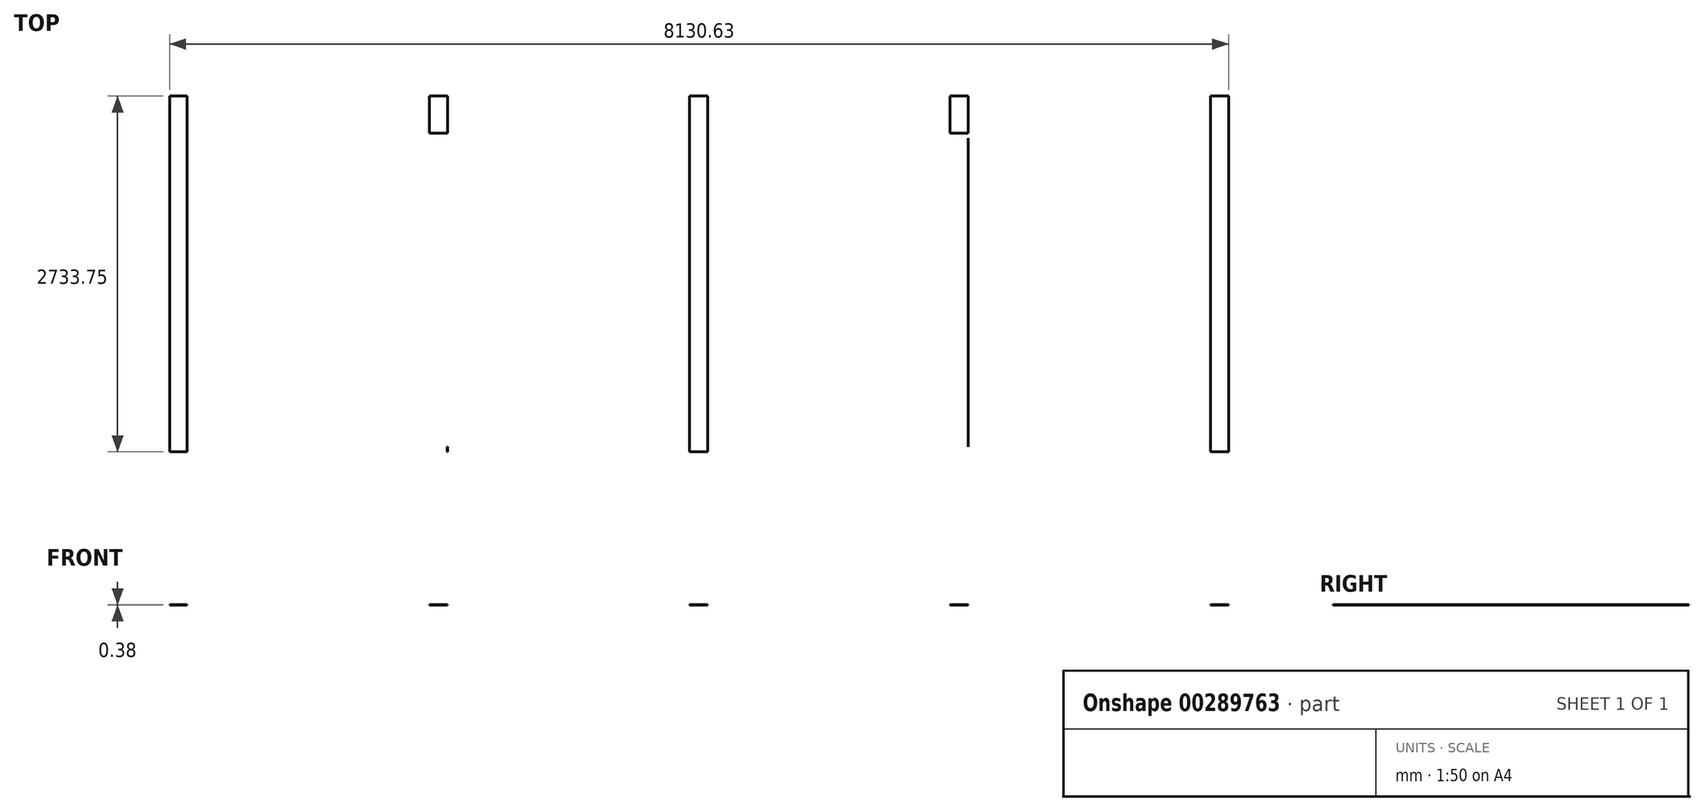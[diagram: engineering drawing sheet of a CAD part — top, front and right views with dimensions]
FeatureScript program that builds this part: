
annotation { "Feature Type Name" : "Feature", "Feature Type Description" : "" }
export const myFeature = defineFeature(function(context is Context, id is Id, definition is map)
    precondition{}
    {
        {
            var Q0;
            Q0=qCreatedBy(makeId("Top.planeOp"),FACE);
            var sketch = newSketch(context, id + "F0", { "sketchPlane" : qUnion([Q0])});
            skLineSegment(sketch, "E0.left", {"start": v(3822.86, -1218.17) * mm, "end": v(3822.86, 1515.58) * mm});
            skLineSegment(sketch, "E1.bottom", {"start": v(-4314.69, -1218.17) * mm, "end": v(3822.86, -1218.17) * mm});
            skLineSegment(sketch, "E2.bottom", {"start": v(3822.86, 1515.58) * mm, "end": v(-245.91, 1515.58) * mm});
            skLineSegment(sketch, "E2.top", {"start": v(3822.86, 1229.83) * mm, "end": v(-245.91, 1229.83) * mm});
            skLineSegment(sketch, "E2.left", {"start": v(3822.86, 1515.58) * mm, "end": v(3822.86, 1229.83) * mm});
            skLineSegment(sketch, "E2.right", {"start": v(-245.91, 1515.58) * mm, "end": v(-245.91, 1229.83) * mm});
            skLineSegment(sketch, "E3", {"start": v(-245.91, 1229.83) * mm, "end": v(-4307.77, 1229.83) * mm});
            skLineSegment(sketch, "E4.bottom", {"start": v(-4307.77, 1229.83) * mm, "end": v(-4168.07, 1229.83) * mm});
            skLineSegment(sketch, "E4.top", {"start": v(-4307.77, -1218.17) * mm, "end": v(-4168.07, -1218.17) * mm});
            skLineSegment(sketch, "E4.left", {"start": v(-4307.77, 1229.83) * mm, "end": v(-4307.77, -1218.17) * mm});
            skLineSegment(sketch, "E4.right", {"start": v(-4168.07, 1229.83) * mm, "end": v(-4168.07, -1218.17) * mm});
            skLineSegment(sketch, "E5.bottom", {"start": v(-315.76, 1229.83) * mm, "end": v(-176.06, 1229.83) * mm});
            skLineSegment(sketch, "E5.top", {"start": v(-315.76, -1218.17) * mm, "end": v(-176.06, -1218.17) * mm});
            skLineSegment(sketch, "E5.left", {"start": v(-315.76, 1229.83) * mm, "end": v(-315.76, -1218.17) * mm});
            skLineSegment(sketch, "E5.right", {"start": v(-176.06, 1229.83) * mm, "end": v(-176.06, -1218.17) * mm});
            skLineSegment(sketch, "E6", {"start": v(-245.91, 1229.83) * mm, "end": v(-245.91, -1218.17) * mm, "construction": true});
            skLineSegment(sketch, "E7.bottom", {"start": v(-2315.25, 1229.83) * mm, "end": v(-2175.55, 1229.83) * mm});
            skLineSegment(sketch, "E7.top", {"start": v(-2315.25, -1218.17) * mm, "end": v(-2175.55, -1218.17) * mm});
            skLineSegment(sketch, "E7.left", {"start": v(-2315.25, 1229.83) * mm, "end": v(-2315.25, -1218.17) * mm});
            skLineSegment(sketch, "E7.right", {"start": v(-2175.55, 1229.83) * mm, "end": v(-2175.55, -1218.17) * mm});
            skLineSegment(sketch, "E8", {"start": v(-4237.92, 1229.83) * mm, "end": v(-4237.92, -1218.17) * mm, "construction": true});
            skLineSegment(sketch, "E9", {"start": v(-2245.4, 1229.83) * mm, "end": v(-2245.4, -1218.17) * mm, "construction": true});
            skLineSegment(sketch, "E10.MirrorCS", {"start": v(3815.94, -1218.17) * mm, "end": v(3676.24, -1218.17) * mm});
            skLineSegment(sketch, "E11.MirrorCS", {"start": v(1823.42, 1229.83) * mm, "end": v(1683.72, 1229.83) * mm});
            skLineSegment(sketch, "E12.MirrorCS", {"start": v(1823.42, -1218.17) * mm, "end": v(1683.72, -1218.17) * mm});
            skLineSegment(sketch, "E13.MirrorCS", {"start": v(3815.94, 1229.83) * mm, "end": v(3676.24, 1229.83) * mm});
            skLineSegment(sketch, "E14.MirrorCS", {"start": v(3815.94, 1229.83) * mm, "end": v(3815.94, -1218.17) * mm});
            skLineSegment(sketch, "E15.MirrorCS", {"start": v(1753.57, 1229.83) * mm, "end": v(1753.57, -1218.17) * mm, "construction": true});
            skLineSegment(sketch, "E16.MirrorCS", {"start": v(1823.42, 1229.83) * mm, "end": v(1823.42, -1218.17) * mm});
            skLineSegment(sketch, "E17.MirrorCS", {"start": v(3746.1, 1229.83) * mm, "end": v(3746.1, -1218.17) * mm, "construction": true});
            skLineSegment(sketch, "E18.MirrorCS", {"start": v(3676.24, 1229.83) * mm, "end": v(3676.24, -1218.17) * mm});
            skLineSegment(sketch, "E19.bottom", {"start": v(-4168.07, -1218.17) * mm, "end": v(-2315.25, -1218.17) * mm});
            skLineSegment(sketch, "E19.top", {"start": v(-4168.07, -1180.07) * mm, "end": v(-2315.25, -1180.07) * mm});
            skLineSegment(sketch, "E19.left", {"start": v(-4168.07, -1218.17) * mm, "end": v(-4168.07, -1180.07) * mm});
            skLineSegment(sketch, "E19.right", {"start": v(-2315.25, -1218.17) * mm, "end": v(-2315.25, -1180.07) * mm});
            skLineSegment(sketch, "E20.bottom", {"start": v(-4168.07, 1229.83) * mm, "end": v(-2315.25, 1229.83) * mm});
            skLineSegment(sketch, "E20.top", {"start": v(-4168.07, 1191.73) * mm, "end": v(-2315.25, 1191.73) * mm});
            skLineSegment(sketch, "E20.left", {"start": v(-4168.07, 1229.83) * mm, "end": v(-4168.07, 1191.73) * mm});
            skLineSegment(sketch, "E20.right", {"start": v(-2315.25, 1229.83) * mm, "end": v(-2315.25, 1191.73) * mm});
            skLineSegment(sketch, "E21.bottom", {"start": v(-4168.07, 1191.73) * mm, "end": v(-4129.97, 1191.73) * mm});
            skLineSegment(sketch, "E21.top", {"start": v(-4168.07, -1180.07) * mm, "end": v(-4129.97, -1180.07) * mm});
            skLineSegment(sketch, "E21.left", {"start": v(-4168.07, 1191.73) * mm, "end": v(-4168.07, -1180.07) * mm});
            skLineSegment(sketch, "E21.right", {"start": v(-4129.97, 1191.73) * mm, "end": v(-4129.97, -1180.07) * mm});
            skLineSegment(sketch, "E22.bottom", {"start": v(-2315.25, 1191.73) * mm, "end": v(-2353.35, 1191.73) * mm});
            skLineSegment(sketch, "E22.top", {"start": v(-2315.25, -1180.07) * mm, "end": v(-2353.35, -1180.07) * mm});
            skLineSegment(sketch, "E22.left", {"start": v(-2315.25, 1191.73) * mm, "end": v(-2315.25, -1180.07) * mm});
            skLineSegment(sketch, "E22.right", {"start": v(-2353.35, 1191.73) * mm, "end": v(-2353.35, -1180.07) * mm});
            skLineSegment(sketch, "E23.bottom", {"start": v(-2759.65, 1191.73) * mm, "end": v(-2721.55, 1191.73) * mm});
            skLineSegment(sketch, "E23.top", {"start": v(-2759.65, -1180.07) * mm, "end": v(-2721.55, -1180.07) * mm});
            skLineSegment(sketch, "E23.left", {"start": v(-2759.65, 1191.73) * mm, "end": v(-2759.65, -1180.07) * mm});
            skLineSegment(sketch, "E23.right", {"start": v(-2721.55, 1191.73) * mm, "end": v(-2721.55, -1180.07) * mm});
            skLineSegment(sketch, "E24.MirrorCS", {"start": v(-2175.55, -1180.07) * mm, "end": v(-2137.45, -1180.07) * mm});
            skLineSegment(sketch, "E25.MirrorCS", {"start": v(-2175.55, -1218.17) * mm, "end": v(-2175.55, -1180.07) * mm});
            skLineSegment(sketch, "E26.MirrorCS", {"start": v(-322.74, -1218.17) * mm, "end": v(-322.74, -1180.07) * mm});
            skLineSegment(sketch, "E27.MirrorCS", {"start": v(-322.74, -1180.07) * mm, "end": v(-360.84, -1180.07) * mm});
            skLineSegment(sketch, "E28.MirrorCS", {"start": v(-322.74, 1191.73) * mm, "end": v(-360.84, 1191.73) * mm});
            skLineSegment(sketch, "E29.MirrorCS", {"start": v(-2175.55, 1229.83) * mm, "end": v(-2175.55, 1191.73) * mm});
            skLineSegment(sketch, "E30.MirrorCS", {"start": v(-2175.55, 1191.73) * mm, "end": v(-2137.45, 1191.73) * mm});
            skLineSegment(sketch, "E31.MirrorCS", {"start": v(-322.74, 1229.83) * mm, "end": v(-322.74, 1191.73) * mm});
            skLineSegment(sketch, "E32.MirrorCS", {"start": v(-512.26, 1191.73) * mm, "end": v(-550.36, 1191.73) * mm});
            skLineSegment(sketch, "E33.MirrorCS", {"start": v(-918.56, -1180.07) * mm, "end": v(-956.66, -1180.07) * mm});
            skLineSegment(sketch, "E34.MirrorCS", {"start": v(-1731.15, 1191.73) * mm, "end": v(-1769.25, 1191.73) * mm});
            skLineSegment(sketch, "E35.MirrorCS", {"start": v(-1324.86, 1191.73) * mm, "end": v(-1362.96, 1191.73) * mm});
            skLineSegment(sketch, "E36.MirrorCS", {"start": v(-918.56, 1191.73) * mm, "end": v(-956.66, 1191.73) * mm});
            skLineSegment(sketch, "E37.MirrorCS", {"start": v(-1731.15, -1180.07) * mm, "end": v(-1769.25, -1180.07) * mm});
            skLineSegment(sketch, "E38.MirrorCS", {"start": v(-512.26, -1180.07) * mm, "end": v(-550.36, -1180.07) * mm});
            skLineSegment(sketch, "E39.MirrorCS", {"start": v(-1324.86, -1180.07) * mm, "end": v(-1362.96, -1180.07) * mm});
            skLineSegment(sketch, "E40.MirrorCS", {"start": v(-322.74, 1191.73) * mm, "end": v(-322.74, -1180.07) * mm});
            skLineSegment(sketch, "E41.MirrorCS", {"start": v(-322.74, -1180.07) * mm, "end": v(-2175.55, -1180.07) * mm});
            skLineSegment(sketch, "E42.MirrorCS", {"start": v(-918.56, 1191.73) * mm, "end": v(-918.56, -1180.07) * mm});
            skLineSegment(sketch, "E43.MirrorCS", {"start": v(-322.74, 1229.83) * mm, "end": v(-2175.55, 1229.83) * mm});
            skLineSegment(sketch, "E44.MirrorCS", {"start": v(-512.26, 1191.73) * mm, "end": v(-512.26, -1180.07) * mm});
            skLineSegment(sketch, "E45.MirrorCS", {"start": v(-360.84, 1191.73) * mm, "end": v(-360.84, -1180.07) * mm});
            skLineSegment(sketch, "E46.MirrorCS", {"start": v(-550.36, 1191.73) * mm, "end": v(-550.36, -1180.07) * mm});
            skLineSegment(sketch, "E47.MirrorCS", {"start": v(-322.74, 1191.73) * mm, "end": v(-2175.55, 1191.73) * mm});
            skLineSegment(sketch, "E48.MirrorCS", {"start": v(-1769.25, 1191.73) * mm, "end": v(-1769.25, -1180.07) * mm});
            skLineSegment(sketch, "E49.MirrorCS", {"start": v(-956.66, 1191.73) * mm, "end": v(-956.66, -1180.07) * mm});
            skLineSegment(sketch, "E50.MirrorCS", {"start": v(-1362.96, 1191.73) * mm, "end": v(-1362.96, -1180.07) * mm});
            skLineSegment(sketch, "E51.MirrorCS", {"start": v(-2175.55, 1191.73) * mm, "end": v(-2175.55, -1180.07) * mm});
            skLineSegment(sketch, "E52.MirrorCS", {"start": v(-322.74, 1229.83) * mm, "end": v(-322.74, -1218.17) * mm});
            skLineSegment(sketch, "E53.MirrorCS", {"start": v(-2137.45, 1191.73) * mm, "end": v(-2137.45, -1180.07) * mm});
            skLineSegment(sketch, "E54.MirrorCS", {"start": v(-1731.15, 1191.73) * mm, "end": v(-1731.15, -1180.07) * mm});
            skLineSegment(sketch, "E55.MirrorCS", {"start": v(-1324.86, 1191.73) * mm, "end": v(-1324.86, -1180.07) * mm});
            skLineSegment(sketch, "E56.MirrorCS", {"start": v(-322.74, -1218.17) * mm, "end": v(-2175.55, -1218.17) * mm});
            skLineSegment(sketch, "E57.MirrorCS", {"start": v(3676.24, -1180.07) * mm, "end": v(3638.14, -1180.07) * mm});
            skLineSegment(sketch, "E58.MirrorCS", {"start": v(3676.24, -1218.17) * mm, "end": v(3676.24, -1180.07) * mm});
            skLineSegment(sketch, "E59.MirrorCS", {"start": v(1823.42, -1218.17) * mm, "end": v(1823.42, -1180.07) * mm});
            skLineSegment(sketch, "E60.MirrorCS", {"start": v(1823.42, 1191.73) * mm, "end": v(1861.52, 1191.73) * mm});
            skLineSegment(sketch, "E61.MirrorCS", {"start": v(3676.24, 1229.83) * mm, "end": v(3676.24, 1191.73) * mm});
            skLineSegment(sketch, "E62.MirrorCS", {"start": v(3676.24, 1191.73) * mm, "end": v(3638.14, 1191.73) * mm});
            skLineSegment(sketch, "E63.MirrorCS", {"start": v(1823.42, -1180.07) * mm, "end": v(1861.52, -1180.07) * mm});
            skLineSegment(sketch, "E64.MirrorCS", {"start": v(1823.42, 1229.83) * mm, "end": v(1823.42, 1191.73) * mm});
            skLineSegment(sketch, "E65.MirrorCS", {"start": v(2267.82, -1180.07) * mm, "end": v(2229.72, -1180.07) * mm});
            skLineSegment(sketch, "E66.MirrorCS", {"start": v(3080.42, 1191.73) * mm, "end": v(3042.32, 1191.73) * mm});
            skLineSegment(sketch, "E67.MirrorCS", {"start": v(3486.72, -1180.07) * mm, "end": v(3448.62, -1180.07) * mm});
            skLineSegment(sketch, "E68.MirrorCS", {"start": v(2674.12, 1191.73) * mm, "end": v(2636.02, 1191.73) * mm});
            skLineSegment(sketch, "E69.MirrorCS", {"start": v(3486.72, 1191.73) * mm, "end": v(3448.62, 1191.73) * mm});
            skLineSegment(sketch, "E70.MirrorCS", {"start": v(2267.82, 1191.73) * mm, "end": v(2229.72, 1191.73) * mm});
            skLineSegment(sketch, "E71.MirrorCS", {"start": v(3080.42, -1180.07) * mm, "end": v(3042.32, -1180.07) * mm});
            skLineSegment(sketch, "E72.MirrorCS", {"start": v(2674.12, -1180.07) * mm, "end": v(2636.02, -1180.07) * mm});
            skLineSegment(sketch, "E73.MirrorCS", {"start": v(3676.24, 1229.83) * mm, "end": v(1823.42, 1229.83) * mm});
            skLineSegment(sketch, "E74.MirrorCS", {"start": v(3676.24, -1218.17) * mm, "end": v(1823.42, -1218.17) * mm});
            skLineSegment(sketch, "E75.MirrorCS", {"start": v(3676.24, 1191.73) * mm, "end": v(3676.24, -1180.07) * mm});
            skLineSegment(sketch, "E76.MirrorCS", {"start": v(1861.52, 1191.73) * mm, "end": v(1861.52, -1180.07) * mm});
            skLineSegment(sketch, "E77.MirrorCS", {"start": v(2229.72, 1191.73) * mm, "end": v(2229.72, -1180.07) * mm});
            skLineSegment(sketch, "E78.MirrorCS", {"start": v(3486.72, 1191.73) * mm, "end": v(3486.72, -1180.07) * mm});
            skLineSegment(sketch, "E79.MirrorCS", {"start": v(3676.24, -1180.07) * mm, "end": v(1823.42, -1180.07) * mm});
            skLineSegment(sketch, "E80.MirrorCS", {"start": v(2674.12, 1191.73) * mm, "end": v(2674.12, -1180.07) * mm});
            skLineSegment(sketch, "E81.MirrorCS", {"start": v(3080.42, 1191.73) * mm, "end": v(3080.42, -1180.07) * mm});
            skLineSegment(sketch, "E82.MirrorCS", {"start": v(3448.62, 1191.73) * mm, "end": v(3448.62, -1180.07) * mm});
            skLineSegment(sketch, "E83.MirrorCS", {"start": v(2267.82, 1191.73) * mm, "end": v(2267.82, -1180.07) * mm});
            skLineSegment(sketch, "E84.MirrorCS", {"start": v(3676.24, 1191.73) * mm, "end": v(1823.42, 1191.73) * mm});
            skLineSegment(sketch, "E85.MirrorCS", {"start": v(1823.42, 1191.73) * mm, "end": v(1823.42, -1180.07) * mm});
            skLineSegment(sketch, "E86.MirrorCS", {"start": v(3638.14, 1191.73) * mm, "end": v(3638.14, -1180.07) * mm});
            skLineSegment(sketch, "E87.MirrorCS", {"start": v(3042.32, 1191.73) * mm, "end": v(3042.32, -1180.07) * mm});
            skLineSegment(sketch, "E88.MirrorCS", {"start": v(-245.91, 1229.83) * mm, "end": v(3815.94, 1229.83) * mm});
            skLineSegment(sketch, "E89.MirrorCS", {"start": v(2636.02, 1191.73) * mm, "end": v(2636.02, -1180.07) * mm});
            skLineSegment(sketch, "E90.left", {"start": v(-176.06, 1191.73) * mm, "end": v(-176.06, 1229.83) * mm});
            skLineSegment(sketch, "E91.top", {"start": v(1645.62, -1180.07) * mm, "end": v(-176.06, -1180.07) * mm});
            skLineSegment(sketch, "E91.right", {"start": v(-176.06, -1218.17) * mm, "end": v(-176.06, -1180.07) * mm});
            skLineSegment(sketch, "E92.bottom", {"start": v(-176.06, 1191.73) * mm, "end": v(-137.96, 1191.73) * mm});
            skLineSegment(sketch, "E92.top", {"start": v(-176.06, -1180.07) * mm, "end": v(-137.96, -1180.07) * mm});
            skLineSegment(sketch, "E92.right", {"start": v(-137.96, 1191.73) * mm, "end": v(-137.96, -1180.07) * mm});
            skLineSegment(sketch, "E93.left", {"start": v(1683.72, 1229.83) * mm, "end": v(1683.72, -1218.17) * mm});
            skLineSegment(sketch, "E94.top", {"start": v(-245.91, 1515.58) * mm, "end": v(-4307.77, 1515.58) * mm});
            skLineSegment(sketch, "E94.left", {"start": v(-245.91, 1229.83) * mm, "end": v(-245.91, 1515.58) * mm});
            skLineSegment(sketch, "E94.right", {"start": v(-4307.77, 1229.83) * mm, "end": v(-4307.77, 1515.58) * mm});
            skLineSegment(sketch, "E95.bottom", {"start": v(-4015.67, -1180.07) * mm, "end": v(-3202.87, -1180.07) * mm});
            skLineSegment(sketch, "E95.top", {"start": v(-4015.67, 591.66) * mm, "end": v(-3202.87, 591.66) * mm});
            skLineSegment(sketch, "E95.left", {"start": v(-4015.67, -1180.07) * mm, "end": v(-4015.67, 591.66) * mm});
            skLineSegment(sketch, "E95.right", {"start": v(-3202.87, -1180.07) * mm, "end": v(-3202.87, 591.66) * mm});
            skLineSegment(sketch, "E96.bottom", {"start": v(-4015.67, 591.66) * mm, "end": v(-4053.77, 591.66) * mm});
            skLineSegment(sketch, "E96.top", {"start": v(-4015.67, -1180.07) * mm, "end": v(-4053.77, -1180.07) * mm});
            skLineSegment(sketch, "E96.left", {"start": v(-4015.67, 591.66) * mm, "end": v(-4015.67, -1180.07) * mm});
            skLineSegment(sketch, "E96.right", {"start": v(-4053.77, 591.66) * mm, "end": v(-4053.77, -1180.07) * mm});
            skLineSegment(sketch, "E97.bottom", {"start": v(-4053.77, -1180.07) * mm, "end": v(-4091.87, -1180.07) * mm});
            skLineSegment(sketch, "E97.top", {"start": v(-4053.77, 1191.73) * mm, "end": v(-4091.87, 1191.73) * mm});
            skLineSegment(sketch, "E97.left", {"start": v(-4053.77, -1180.07) * mm, "end": v(-4053.77, 1191.73) * mm});
            skLineSegment(sketch, "E97.right", {"start": v(-4091.87, -1180.07) * mm, "end": v(-4091.87, 1191.73) * mm});
            skLineSegment(sketch, "E98.bottom", {"start": v(-3202.87, 591.66) * mm, "end": v(-3164.77, 591.66) * mm});
            skLineSegment(sketch, "E98.top", {"start": v(-3202.87, -1180.07) * mm, "end": v(-3164.77, -1180.07) * mm});
            skLineSegment(sketch, "E98.left", {"start": v(-3202.87, 591.66) * mm, "end": v(-3202.87, -1180.07) * mm});
            skLineSegment(sketch, "E98.right", {"start": v(-3164.77, 591.66) * mm, "end": v(-3164.77, -1180.07) * mm});
            skLineSegment(sketch, "E99.bottom", {"start": v(-3164.77, -1180.07) * mm, "end": v(-3126.67, -1180.07) * mm});
            skLineSegment(sketch, "E99.top", {"start": v(-3164.77, 1191.73) * mm, "end": v(-3126.67, 1191.73) * mm});
            skLineSegment(sketch, "E99.left", {"start": v(-3164.77, -1180.07) * mm, "end": v(-3164.77, 1191.73) * mm});
            skLineSegment(sketch, "E99.right", {"start": v(-3126.67, -1180.07) * mm, "end": v(-3126.67, 1191.73) * mm});
            skLineSegment(sketch, "E100.bottom", {"start": v(-3164.77, 591.66) * mm, "end": v(-4053.77, 591.66) * mm});
            skLineSegment(sketch, "E100.top", {"start": v(-3164.77, 629.76) * mm, "end": v(-4053.77, 629.76) * mm});
            skLineSegment(sketch, "E100.left", {"start": v(-3164.77, 591.66) * mm, "end": v(-3164.77, 629.76) * mm});
            skLineSegment(sketch, "E100.right", {"start": v(-4053.77, 591.66) * mm, "end": v(-4053.77, 629.76) * mm});
            skLineSegment(sketch, "E101", {"start": v(-3609.27, 629.76) * mm, "end": v(-3609.27, 1191.73) * mm, "construction": true});
            skLineSegment(sketch, "E102.bottom", {"start": v(-3628.47, 629.76) * mm, "end": v(-3590.07, 629.76) * mm});
            skLineSegment(sketch, "E102.top", {"start": v(-3628.47, 1191.73) * mm, "end": v(-3590.07, 1191.73) * mm});
            skLineSegment(sketch, "E102.left", {"start": v(-3628.47, 629.76) * mm, "end": v(-3628.47, 1191.73) * mm});
            skLineSegment(sketch, "E102.right", {"start": v(-3590.07, 629.76) * mm, "end": v(-3590.07, 1191.73) * mm});
            skLineSegment(sketch, "E103.bottom", {"start": v(-3860.12, 1191.73) * mm, "end": v(-3822.02, 1191.73) * mm});
            skLineSegment(sketch, "E103.top", {"start": v(-3860.12, 629.76) * mm, "end": v(-3822.02, 629.76) * mm});
            skLineSegment(sketch, "E103.left", {"start": v(-3860.12, 1191.73) * mm, "end": v(-3860.12, 629.76) * mm});
            skLineSegment(sketch, "E103.right", {"start": v(-3822.02, 1191.73) * mm, "end": v(-3822.02, 629.76) * mm});
            skLineSegment(sketch, "E104", {"start": v(-3841.07, 1191.73) * mm, "end": v(-3841.07, 629.76) * mm, "construction": true});
            skLineSegment(sketch, "E105.MirrorCS", {"start": v(-3358.42, 1191.73) * mm, "end": v(-3358.42, 629.76) * mm});
            skLineSegment(sketch, "E106.MirrorCS", {"start": v(-3396.52, 1191.73) * mm, "end": v(-3396.52, 629.76) * mm});
            skLineSegment(sketch, "E107", {"start": v(-3202.87, -1180.07) * mm, "end": v(-3202.87, -1218.17) * mm});
            skLineSegment(sketch, "E108", {"start": v(-4015.67, -1180.07) * mm, "end": v(-4015.67, -1218.17) * mm});
            skLineSegment(sketch, "E109.right", {"start": v(1645.62, 1191.73) * mm, "end": v(1645.62, -1218.17) * mm});
            skLineSegment(sketch, "E110", {"start": v(1683.72, 1229.83) * mm, "end": v(1683.72, 1229.83) * mm});
            skLineSegment(sketch, "E111", {"start": v(-137.96, 1191.73) * mm, "end": v(1645.62, 1191.73) * mm});
            skLineSegment(sketch, "E112.bottom", {"start": v(-137.96, 877.33) * mm, "end": v(-99.86, 877.33) * mm});
            skLineSegment(sketch, "E112.top", {"start": v(-137.96, -1180.07) * mm, "end": v(-99.86, -1180.07) * mm});
            skLineSegment(sketch, "E112.left", {"start": v(-137.96, 877.33) * mm, "end": v(-137.96, -1180.07) * mm});
            skLineSegment(sketch, "E112.right", {"start": v(-99.86, 877.33) * mm, "end": v(-99.86, -1180.07) * mm});
            skLineSegment(sketch, "E113.bottom", {"start": v(-137.96, 877.33) * mm, "end": v(916.14, 877.33) * mm});
            skLineSegment(sketch, "E113.top", {"start": v(-137.96, 915.43) * mm, "end": v(916.14, 915.43) * mm});
            skLineSegment(sketch, "E113.left", {"start": v(-137.96, 877.33) * mm, "end": v(-137.96, 915.43) * mm});
            skLineSegment(sketch, "E113.right", {"start": v(916.14, 877.33) * mm, "end": v(916.14, 915.43) * mm});
            skLineSegment(sketch, "E114", {"start": v(878.04, 877.33) * mm, "end": v(878.04, -1218.17) * mm});
            skLineSegment(sketch, "E115.bottom", {"start": v(916.14, 1191.73) * mm, "end": v(954.24, 1191.73) * mm});
            skLineSegment(sketch, "E115.top", {"start": v(916.14, -1180.07) * mm, "end": v(954.24, -1180.07) * mm});
            skLineSegment(sketch, "E115.left", {"start": v(916.14, 1191.73) * mm, "end": v(916.14, -1180.07) * mm});
            skLineSegment(sketch, "E115.right", {"start": v(954.24, 1191.73) * mm, "end": v(954.24, -1180.07) * mm});
            skLineSegment(sketch, "E116", {"start": v(389.09, 915.43) * mm, "end": v(389.09, 1191.73) * mm, "construction": true});
            skLineSegment(sketch, "E117.bottom", {"start": v(369.88, 1191.73) * mm, "end": v(408.29, 1191.73) * mm});
            skLineSegment(sketch, "E117.top", {"start": v(369.88, 915.43) * mm, "end": v(408.29, 915.43) * mm});
            skLineSegment(sketch, "E117.left", {"start": v(369.88, 1191.73) * mm, "end": v(369.88, 915.43) * mm});
            skLineSegment(sketch, "E117.right", {"start": v(408.29, 1191.73) * mm, "end": v(408.29, 915.43) * mm});
            skLineSegment(sketch, "E118.bottom", {"start": v(96.94, 915.43) * mm, "end": v(135.04, 915.43) * mm});
            skLineSegment(sketch, "E118.top", {"start": v(96.94, 1191.73) * mm, "end": v(135.04, 1191.73) * mm});
            skLineSegment(sketch, "E118.left", {"start": v(96.94, 915.43) * mm, "end": v(96.94, 1191.73) * mm});
            skLineSegment(sketch, "E118.right", {"start": v(135.04, 915.43) * mm, "end": v(135.04, 1191.73) * mm});
            skLineSegment(sketch, "E119", {"start": v(115.99, 1191.73) * mm, "end": v(115.99, 915.43) * mm, "construction": true});
            skLineSegment(sketch, "E120.MirrorCS", {"start": v(681.24, 1191.73) * mm, "end": v(643.14, 1191.73) * mm});
            skLineSegment(sketch, "E121.MirrorCS", {"start": v(681.24, 915.43) * mm, "end": v(643.14, 915.43) * mm});
            skLineSegment(sketch, "E122.MirrorCS", {"start": v(643.14, 915.43) * mm, "end": v(643.14, 1191.73) * mm});
            skLineSegment(sketch, "E123.MirrorCS", {"start": v(662.19, 1191.73) * mm, "end": v(662.19, 915.43) * mm, "construction": true});
            skLineSegment(sketch, "E124.MirrorCS", {"start": v(681.24, 915.43) * mm, "end": v(681.24, 1191.73) * mm});
            skLineSegment(sketch, "E125.bottom", {"start": v(1322.43, 1191.73) * mm, "end": v(1360.53, 1191.73) * mm});
            skLineSegment(sketch, "E125.top", {"start": v(1322.43, -1180.07) * mm, "end": v(1360.53, -1180.07) * mm});
            skLineSegment(sketch, "E125.left", {"start": v(1322.43, 1191.73) * mm, "end": v(1322.43, -1180.07) * mm});
            skLineSegment(sketch, "E125.right", {"start": v(1360.53, 1191.73) * mm, "end": v(1360.53, -1180.07) * mm});
            skLineSegment(sketch, "E126", {"start": v(-99.86, -1180.07) * mm, "end": v(-99.86, -1218.17) * mm});
            skSolve(sketch);
        }
        {
            var Q0;
            {var subQ3=sQuery(id+"F0.wireOp",EDGE,"jjNAWN9L-icPI-AxbA-Y6Pq-o1EGEALKaFy1");var subQ5=sQuery(id+"F0.wireOp",EDGE,"5f963c61-5f66-4834-8852-3989dfd0aaaa0.MirrorCS");var subQ6=makeQuery(id+"F0.imprint","INTERSECT",VERTEX,{"derivedFrom":[subQ5,subQ3]});Q0=makeQuery(id+"F0.imprint","IMPRINT",FACE,{"disambiguationData":[TD([[makeQuery(id+"F0.imprint","IMPRINT",EDGE,{"disambiguationData":[TD([[subQ6,-1.0]])],"derivedFrom":subQ5}),-1.0]])]});}
            var Q1;
            {var subQ1=sQuery(id+"F0.wireOp",EDGE,"c3f41723-229c-4d74-ac07-4786d7f9cf2e0.MirrorCS");var subQ5=sQuery(id+"F0.wireOp",EDGE,"jjNAWN9L-icPI-AxbA-Y6Pq-o1EGEALKaFy1");var subQ7=makeQuery(id+"F0.imprint","INTERSECT",VERTEX,{"derivedFrom":[subQ1,subQ5]});Q1=makeQuery(id+"F0.imprint","IMPRINT",FACE,{"disambiguationData":[TD([[makeQuery(id+"F0.imprint","IMPRINT",EDGE,{"disambiguationData":[TD([[subQ7,-1.0]])],"derivedFrom":subQ1}),1.0]])]});}
            var Q2;
            {var subQ5=sQuery(id+"F0.wireOp",EDGE,"lJZTp2Bh-KL5G-mgcu-Pd3p-ZrVlOJJElSC5");Q2=makeQuery(id+"F0.imprint","IMPRINT",FACE,{"disambiguationData":[TD([[makeQuery(id+"F0.imprint","IMPRINT",EDGE,{"derivedFrom":subQ5}),1.0]])]});}
            var Q3;
            {var subQ0=sQuery(id+"F0.wireOp",EDGE,"1XwIb5Eg-bF9u-TIWm-DKcX-weKEORKnCqGm.right");Q3=makeQuery(id+"F0.imprint","IMPRINT",FACE,{"disambiguationData":[TD([[makeQuery(id+"F0.imprint","IMPRINT",EDGE,{"derivedFrom":subQ0}),-1.0]])]});}
            var Q4;
            {var subQ0=sQuery(id+"F0.wireOp",EDGE,"edbdd21b-7951-4497-ac7e-6e46abb4ccd70.MirrorCS");Q4=makeQuery(id+"F0.imprint","IMPRINT",FACE,{"disambiguationData":[TD([[makeQuery(id+"F0.imprint","IMPRINT",EDGE,{"derivedFrom":subQ0}),-1.0]])]});}
            var Q5;
            {var subQ0=sQuery(id+"F0.wireOp",EDGE,"573c87d8-b675-496e-a079-9395e3357b8d0.MirrorCS");Q5=makeQuery(id+"F0.imprint","IMPRINT",FACE,{"disambiguationData":[TD([[makeQuery(id+"F0.imprint","IMPRINT",EDGE,{"derivedFrom":subQ0}),1.0]])]});}
            var Q6;
            {var subQ0=sQuery(id+"F0.wireOp",EDGE,"7de17b8e-8469-475a-b975-fd82b060c23f0.MirrorCS");Q6=makeQuery(id+"F0.imprint","IMPRINT",FACE,{"disambiguationData":[TD([[makeQuery(id+"F0.imprint","IMPRINT",EDGE,{"derivedFrom":subQ0}),1.0]])]});}
            var Q7;
            {var subQ0=sQuery(id+"F0.wireOp",EDGE,"9fe0fe99-07bc-4679-9664-f55d6f2dc43d0.MirrorCS");Q7=makeQuery(id+"F0.imprint","IMPRINT",FACE,{"disambiguationData":[TD([[makeQuery(id+"F0.imprint","IMPRINT",EDGE,{"derivedFrom":subQ0}),1.0]])]});}
            var Q8;
            {var subQ0=sQuery(id+"F0.wireOp",EDGE,"b7a96eb8-1ea0-4e2f-8a00-b5aa0dec934b0.MirrorCS");Q8=makeQuery(id+"F0.imprint","IMPRINT",FACE,{"disambiguationData":[TD([[makeQuery(id+"F0.imprint","IMPRINT",EDGE,{"derivedFrom":subQ0}),-1.0]])]});}
            var Q9;
            {var subQ0=sQuery(id+"F0.wireOp",EDGE,"e03bbd14-4e46-43d8-a5f9-80b2dea7db7f0.MirrorCS");Q9=makeQuery(id+"F0.imprint","IMPRINT",FACE,{"disambiguationData":[TD([[makeQuery(id+"F0.imprint","IMPRINT",EDGE,{"derivedFrom":subQ0}),1.0]])]});}
            var Q10;
            {var subQ5=sQuery(id+"F0.wireOp",EDGE,"0632b321-56e7-4b31-9cd1-585e07a893ff0.MirrorCS");var subQ6=sQuery(id+"F0.wireOp",EDGE,"1XwIb5Eg-bF9u-TIWm-DKcX-weKEORKnCqGm.bottom");var subQ7=makeQuery(id+"F0.imprint","INTERSECT",VERTEX,{"derivedFrom":[subQ6,subQ5]});Q10=makeQuery(id+"F0.imprint","IMPRINT",FACE,{"disambiguationData":[TD([[makeQuery(id+"F0.imprint","IMPRINT",EDGE,{"disambiguationData":[TD([[subQ7,-1.0]])],"derivedFrom":subQ6}),-1.0]])]});}
            var Q11;
            Q11=makeQuery(id+"F0.imprint","IMPRINT",FACE,{"disambiguationData":[TD([[makeQuery(id+"F0.imprint","IMPRINT",EDGE,{"derivedFrom":sQuery(id+"F0.wireOp",EDGE,"w7in2STq-dmfq-Ztst-uc13-PS53EKAe34f7.bottom")}),-1.0]])]});
            var Q12;
            {var subQ4=sQuery(id+"F0.wireOp",EDGE,"019fe33c-2ba7-4981-a1aa-b8912489248e0.MirrorCS");var subQ6=sQuery(id+"F0.wireOp",EDGE,"1XwIb5Eg-bF9u-TIWm-DKcX-weKEORKnCqGm.bottom");var subQ7=makeQuery(id+"F0.imprint","INTERSECT",VERTEX,{"derivedFrom":[subQ6,subQ4]});Q12=makeQuery(id+"F0.imprint","IMPRINT",FACE,{"disambiguationData":[TD([[makeQuery(id+"F0.imprint","IMPRINT",EDGE,{"disambiguationData":[TD([[subQ7,-1.0]])],"derivedFrom":subQ6}),-1.0]])]});}
            var Q13;
            {var subQ5=sQuery(id+"F0.wireOp",EDGE,"E1.right");Q13=makeQuery(id+"F0.imprint","IMPRINT",FACE,{"disambiguationData":[TD([[makeQuery(id+"F0.imprint","IMPRINT",EDGE,{"derivedFrom":subQ5}),1.0]])]});}
            var Q14;
            {var subQ4=sQuery(id+"F0.wireOp",EDGE,"8a681850-bd4a-4ca6-8d45-30870cc5114b0.MirrorCS");var subQ6=sQuery(id+"F0.wireOp",EDGE,"1XwIb5Eg-bF9u-TIWm-DKcX-weKEORKnCqGm.bottom");var subQ7=makeQuery(id+"F0.imprint","INTERSECT",VERTEX,{"derivedFrom":[subQ6,subQ4]});Q14=makeQuery(id+"F0.imprint","IMPRINT",FACE,{"disambiguationData":[TD([[makeQuery(id+"F0.imprint","IMPRINT",EDGE,{"disambiguationData":[TD([[subQ7,-1.0]])],"derivedFrom":subQ6}),-1.0]])]});}
            var Q15;
            {var subQ4=sQuery(id+"F0.wireOp",EDGE,"1XwIb5Eg-bF9u-TIWm-DKcX-weKEORKnCqGm.left");Q15=makeQuery(id+"F0.imprint","IMPRINT",FACE,{"disambiguationData":[TD([[makeQuery(id+"F0.imprint","IMPRINT",EDGE,{"derivedFrom":subQ4}),1.0]])]});}
            var Q16;
            {var subQ5=sQuery(id+"F0.wireOp",EDGE,"1XwIb5Eg-bF9u-TIWm-DKcX-weKEORKnCqGm.bottom");var subQ11=sQuery(id+"F0.wireOp",EDGE,"f7381abf-e9df-4e1a-a30e-4fe6b1d368c50.MirrorCS");var subQ12=makeQuery(id+"F0.imprint","INTERSECT",VERTEX,{"derivedFrom":[subQ5,subQ11]});Q16=makeQuery(id+"F0.imprint","IMPRINT",FACE,{"disambiguationData":[TD([[makeQuery(id+"F0.imprint","IMPRINT",EDGE,{"disambiguationData":[TD([[subQ12,-1.0]])],"derivedFrom":subQ5}),-1.0]])]});}
            var Q17;
            {var subQ6=sQuery(id+"F0.wireOp",EDGE,"E1.left");Q17=makeQuery(id+"F0.imprint","IMPRINT",FACE,{"disambiguationData":[TD([[makeQuery(id+"F0.imprint","IMPRINT",EDGE,{"derivedFrom":subQ6}),-1.0]])]});}
            var Q18;
            {var subQ6=sQuery(id+"F0.wireOp",EDGE,"5OPExjK1-Sqdo-9fgj-zmjT-l9LixJuiSe1q");Q18=makeQuery(id+"F0.imprint","IMPRINT",FACE,{"disambiguationData":[TD([[makeQuery(id+"F0.imprint","IMPRINT",EDGE,{"derivedFrom":subQ6}),-1.0]])]});}
            var Q19;
            {var subQ0=sQuery(id+"F0.wireOp",EDGE,"95ca570f-170f-43a6-b84c-d3a65055c82b0.MirrorCS");Q19=makeQuery(id+"F0.imprint","IMPRINT",FACE,{"disambiguationData":[TD([[makeQuery(id+"F0.imprint","IMPRINT",EDGE,{"derivedFrom":subQ0}),1.0]])]});}
            var Q20;
            {var subQ3=sQuery(id+"F0.wireOp",EDGE,"eca8af08-4f88-4f9e-b7fb-055b73c8b4f30.MirrorCS");var subQ4=sQuery(id+"F0.wireOp",EDGE,"1XwIb5Eg-bF9u-TIWm-DKcX-weKEORKnCqGm.bottom");var subQ5=makeQuery(id+"F0.imprint","INTERSECT",VERTEX,{"derivedFrom":[subQ4,subQ3]});Q20=makeQuery(id+"F0.imprint","IMPRINT",FACE,{"disambiguationData":[TD([[makeQuery(id+"F0.imprint","IMPRINT",EDGE,{"disambiguationData":[TD([[subQ5,-1.0]])],"derivedFrom":subQ4}),-1.0]])]});}
            var Q21;
            {var subQ0=sQuery(id+"F0.wireOp",EDGE,"1XwIb5Eg-bF9u-TIWm-DKcX-weKEORKnCqGm.right");Q21=makeQuery(id+"F0.imprint","IMPRINT",FACE,{"disambiguationData":[TD([[makeQuery(id+"F0.imprint","IMPRINT",EDGE,{"derivedFrom":subQ0}),-1.0]])]});}
            var Q22;
            {var subQ7=sQuery(id+"F0.wireOp",EDGE,"7E0FlCXR-JigA-jfUJ-zGrG-kKcglUNU7Liy");Q22=makeQuery(id+"F0.imprint","IMPRINT",FACE,{"disambiguationData":[TD([[makeQuery(id+"F0.imprint","IMPRINT",EDGE,{"derivedFrom":subQ7}),-1.0]])]});}
            var Q23;
            {var subQ4=sQuery(id+"F0.wireOp",EDGE,"1bcce820-757c-45ce-a4fe-54bff22ba8310.MirrorCS");var subQ5=sQuery(id+"F0.wireOp",EDGE,"1XwIb5Eg-bF9u-TIWm-DKcX-weKEORKnCqGm.bottom");var subQ6=makeQuery(id+"F0.imprint","INTERSECT",VERTEX,{"derivedFrom":[subQ5,subQ4]});Q23=makeQuery(id+"F0.imprint","IMPRINT",FACE,{"disambiguationData":[TD([[makeQuery(id+"F0.imprint","IMPRINT",EDGE,{"disambiguationData":[TD([[subQ6,-1.0]])],"derivedFrom":subQ5}),-1.0]])]});}
            var Q24;
            Q24=makeQuery(id+"F0.imprint","IMPRINT",FACE,{"disambiguationData":[TD([[makeQuery(id+"F0.imprint","IMPRINT",EDGE,{"derivedFrom":sQuery(id+"F0.wireOp",EDGE,"xTM1oSQN-q9p7-LrQJ-wgkP-syFjsQtJfwuK.bottom")}),-1.0]])]});
            var Q25;
            {var subQ0=sQuery(id+"F0.wireOp",EDGE,"1b0e9755-274d-47f2-9ad2-c5868fe4f0aa0.MirrorCS");Q25=makeQuery(id+"F0.imprint","IMPRINT",FACE,{"disambiguationData":[TD([[makeQuery(id+"F0.imprint","IMPRINT",EDGE,{"derivedFrom":subQ0}),1.0]])]});}
            var Q26;
            {var subQ0=sQuery(id+"F0.wireOp",EDGE,"2c59450c-3f31-460a-8c07-403c14a947670.MirrorCS");Q26=makeQuery(id+"F0.imprint","IMPRINT",FACE,{"disambiguationData":[TD([[makeQuery(id+"F0.imprint","IMPRINT",EDGE,{"derivedFrom":subQ0}),1.0]])]});}
            var Q27;
            {var subQ0=sQuery(id+"F0.wireOp",EDGE,"1b9fc814-7275-47f6-8dd0-aeae657b9ac90.MirrorCS");Q27=makeQuery(id+"F0.imprint","IMPRINT",FACE,{"disambiguationData":[TD([[makeQuery(id+"F0.imprint","IMPRINT",EDGE,{"derivedFrom":subQ0}),1.0]])]});}
            var Q28;
            {var subQ0=sQuery(id+"F0.wireOp",EDGE,"0493b29f-ec4a-4c4c-ac9e-8fdb3be76d310.MirrorCS");Q28=makeQuery(id+"F0.imprint","IMPRINT",FACE,{"disambiguationData":[TD([[makeQuery(id+"F0.imprint","IMPRINT",EDGE,{"derivedFrom":subQ0}),1.0]])]});}
            var Q29;
            {var subQ0=sQuery(id+"F0.wireOp",EDGE,"63c733ed-a5aa-43e7-ab23-9ab8c604324c0.MirrorCS");Q29=makeQuery(id+"F0.imprint","IMPRINT",FACE,{"disambiguationData":[TD([[makeQuery(id+"F0.imprint","IMPRINT",EDGE,{"derivedFrom":subQ0}),1.0]])]});}
            var Q30;
            Q30=makeQuery(id+"F0.imprint","IMPRINT",FACE,{"disambiguationData":[TD([[makeQuery(id+"F0.imprint","IMPRINT",EDGE,{"derivedFrom":sQuery(id+"F0.wireOp",EDGE,"3EoNbSYs-SzWb-u8DF-ybgV-jMauNVkNRy9z.bottom")}),1.0]])]});
            var Q31;
            {var subQ0=sQuery(id+"F0.wireOp",EDGE,"T9lHoMTv-QEzR-Dyhh-EcdA-VJLsKytDJrYi");Q31=makeQuery(id+"F0.imprint","IMPRINT",FACE,{"disambiguationData":[TD([[makeQuery(id+"F0.imprint","IMPRINT",EDGE,{"derivedFrom":subQ0}),1.0]])]});}
            var Q32;
            {var subQ0=sQuery(id+"F0.wireOp",EDGE,"e8148a9c-46db-40cc-98a3-4964df314f830.MirrorCS");Q32=makeQuery(id+"F0.imprint","IMPRINT",FACE,{"disambiguationData":[TD([[makeQuery(id+"F0.imprint","IMPRINT",EDGE,{"derivedFrom":subQ0}),-1.0]])]});}
            var Q33;
            {var subQ6=sQuery(id+"F0.wireOp",EDGE,"sNmUnq7e-THn6-FXXE-0TdV-tI3yUDcPX31l");Q33=makeQuery(id+"F0.imprint","IMPRINT",FACE,{"disambiguationData":[TD([[makeQuery(id+"F0.imprint","IMPRINT",EDGE,{"derivedFrom":subQ6}),1.0]])]});}
            var Q34;
            {var subQ0=sQuery(id+"F0.wireOp",EDGE,"TX6lwSvD-SgXL-Km0w-BdGv-l82Iv6GDQNNj");Q34=makeQuery(id+"F0.imprint","IMPRINT",FACE,{"disambiguationData":[TD([[makeQuery(id+"F0.imprint","IMPRINT",EDGE,{"derivedFrom":subQ0}),1.0]])]});}
            var Q35;
            {var subQ5=sQuery(id+"F0.wireOp",EDGE,"lJZTp2Bh-KL5G-mgcu-Pd3p-ZrVlOJJElSC5");Q35=makeQuery(id+"F0.imprint","IMPRINT",FACE,{"disambiguationData":[TD([[makeQuery(id+"F0.imprint","IMPRINT",EDGE,{"derivedFrom":subQ5}),1.0]])]});}
            var Q36;
            {var subQ3=sQuery(id+"F0.wireOp",EDGE,"7Q4NYOsG-TNh0-UE7v-idsB-Km2WiAvK161E");Q36=makeQuery(id+"F0.imprint","IMPRINT",FACE,{"disambiguationData":[TD([[makeQuery(id+"F0.imprint","IMPRINT",EDGE,{"derivedFrom":subQ3}),1.0]])]});}
            var Q37;
            {var subQ5=sQuery(id+"F0.wireOp",EDGE,"lJZTp2Bh-KL5G-mgcu-Pd3p-ZrVlOJJElSC5");Q37=makeQuery(id+"F0.imprint","IMPRINT",FACE,{"disambiguationData":[TD([[makeQuery(id+"F0.imprint","IMPRINT",EDGE,{"derivedFrom":subQ5}),1.0]])]});}
            var Q38;
            {var subQ6=sQuery(id+"F0.wireOp",EDGE,"5OPExjK1-Sqdo-9fgj-zmjT-l9LixJuiSe1q");Q38=makeQuery(id+"F0.imprint","IMPRINT",FACE,{"disambiguationData":[TD([[makeQuery(id+"F0.imprint","IMPRINT",EDGE,{"derivedFrom":subQ6}),-1.0]])]});}
            var Q39;
            {var subQ3=sQuery(id+"F0.wireOp",EDGE,"kb0NHO8k-GRdv-KMOx-osSm-lJc2wDgV5qJY");Q39=makeQuery(id+"F0.imprint","IMPRINT",FACE,{"disambiguationData":[TD([[makeQuery(id+"F0.imprint","IMPRINT",EDGE,{"derivedFrom":subQ3}),1.0]])]});}
            var Q40;
            {var subQ0=sQuery(id+"F0.wireOp",EDGE,"n8L3RjNa-mBsY-hc5F-DRgW-xquJLlsyQC8t");var subQ1=sQuery(id+"F0.wireOp",EDGE,"019fe33c-2ba7-4981-a1aa-b8912489248e0.MirrorCS");var subQ2=makeQuery(id+"F0.imprint","INTERSECT",VERTEX,{"derivedFrom":[subQ1,subQ0]});Q40=makeQuery(id+"F0.imprint","IMPRINT",FACE,{"disambiguationData":[TD([[makeQuery(id+"F0.imprint","IMPRINT",EDGE,{"disambiguationData":[TD([[subQ2,-1.0]])],"derivedFrom":subQ1}),-1.0]])]});}
            var Q41;
            {var subQ6=sQuery(id+"F0.wireOp",EDGE,"5OPExjK1-Sqdo-9fgj-zmjT-l9LixJuiSe1q");Q41=makeQuery(id+"F0.imprint","IMPRINT",FACE,{"disambiguationData":[TD([[makeQuery(id+"F0.imprint","IMPRINT",EDGE,{"derivedFrom":subQ6}),-1.0]])]});}
            var Q42;
            {var subQ0=sQuery(id+"F0.wireOp",EDGE,"0e344b7f-dcc7-4a3f-8939-196222c3ee7a0.MirrorCS");Q42=makeQuery(id+"F0.imprint","IMPRINT",FACE,{"disambiguationData":[TD([[makeQuery(id+"F0.imprint","IMPRINT",EDGE,{"derivedFrom":subQ0}),-1.0]])]});}
            var Q43;
            {var subQ0=sQuery(id+"F0.wireOp",EDGE,"Bkj7O7oP-ktTF-DsHg-vzrG-3IRV2kZJSDV0");var subQ5=sQuery(id+"F0.wireOp",EDGE,"E1.top");var subQ8=makeQuery(id+"F0.imprint","INTERSECT",VERTEX,{"derivedFrom":[subQ5,subQ0]});Q43=makeQuery(id+"F0.imprint","IMPRINT",FACE,{"disambiguationData":[TD([[makeQuery(id+"F0.imprint","IMPRINT",EDGE,{"disambiguationData":[TD([[subQ8,-1.0]])],"derivedFrom":subQ5}),1.0]])]});}
            var Q44;
            {var subQ0=sQuery(id+"F0.wireOp",EDGE,"jjNAWN9L-icPI-AxbA-Y6Pq-o1EGEALKaFy1");var subQ1=sQuery(id+"F0.wireOp",EDGE,"eaf639a9-24cc-49c5-a44c-8973cc1609e50.MirrorCS");var subQ2=makeQuery(id+"F0.imprint","INTERSECT",VERTEX,{"derivedFrom":[subQ1,subQ0]});Q44=makeQuery(id+"F0.imprint","IMPRINT",FACE,{"disambiguationData":[TD([[makeQuery(id+"F0.imprint","IMPRINT",EDGE,{"disambiguationData":[TD([[subQ2,-1.0]])],"derivedFrom":subQ1}),1.0]])]});}
            var Q45;
            Q45=makeQuery(id+"F0.imprint","IMPRINT",FACE,{"disambiguationData":[TD([[makeQuery(id+"F0.imprint","IMPRINT",EDGE,{"derivedFrom":sQuery(id+"F0.wireOp",EDGE,"E4.bottom")}),-1.0]])]});
            var Q46;
            Q46=makeQuery(id+"F0.imprint","IMPRINT",FACE,{"disambiguationData":[TD([[makeQuery(id+"F0.imprint","IMPRINT",EDGE,{"derivedFrom":sQuery(id+"F0.wireOp",EDGE,"E21.bottom")}),-1.0]])]});
            var Q47;
            Q47=makeQuery(id+"F0.imprint","IMPRINT",FACE,{"disambiguationData":[TD([[makeQuery(id+"F0.imprint","IMPRINT",EDGE,{"derivedFrom":sQuery(id+"F0.wireOp",EDGE,"E20.bottom")}),-1.0]])]});
            var Q48;
            Q48=makeQuery(id+"F0.imprint","IMPRINT",FACE,{"disambiguationData":[TD([[makeQuery(id+"F0.imprint","IMPRINT",EDGE,{"derivedFrom":sQuery(id+"F0.wireOp",EDGE,"V0uafj4D-blUL-0R42-RDYG-w4zu7gxU5Okz.bottom")}),-1.0]])]});
            var Q49;
            Q49=makeQuery(id+"F0.imprint","IMPRINT",FACE,{"disambiguationData":[TD([[makeQuery(id+"F0.imprint","IMPRINT",EDGE,{"derivedFrom":sQuery(id+"F0.wireOp",EDGE,"tgIF31wR-Pcny-3N63-f3Ax-q6FNio27vSr7.bottom")}),-1.0]])]});
            var Q50;
            Q50=makeQuery(id+"F0.imprint","IMPRINT",FACE,{"disambiguationData":[TD([[makeQuery(id+"F0.imprint","IMPRINT",EDGE,{"derivedFrom":sQuery(id+"F0.wireOp",EDGE,"tej6zg4S-c0JJ-q25J-w4bm-2LaaiJUFbgIA.bottom")}),-1.0]])]});
            var Q51;
            Q51=makeQuery(id+"F0.imprint","IMPRINT",FACE,{"disambiguationData":[TD([[makeQuery(id+"F0.imprint","IMPRINT",EDGE,{"derivedFrom":sQuery(id+"F0.wireOp",EDGE,"E23.bottom")}),-1.0]])]});
            var Q52;
            Q52=makeQuery(id+"F0.imprint","IMPRINT",FACE,{"disambiguationData":[TD([[makeQuery(id+"F0.imprint","IMPRINT",EDGE,{"derivedFrom":sQuery(id+"F0.wireOp",EDGE,"E22.bottom")}),1.0]])]});
            var Q53;
            {var subQ2=sQuery(id+"F0.wireOp",EDGE,"E7.bottom");Q53=makeQuery(id+"F0.imprint","IMPRINT",FACE,{"disambiguationData":[TD([[makeQuery(id+"F0.imprint","IMPRINT",EDGE,{"derivedFrom":subQ2}),-1.0]])]});}
            var Q54;
            {var subQ3=sQuery(id+"F0.wireOp",EDGE,"E19.left");Q54=makeQuery(id+"F0.imprint","IMPRINT",FACE,{"disambiguationData":[TD([[makeQuery(id+"F0.imprint","IMPRINT",EDGE,{"derivedFrom":subQ3}),-1.0]])]});}
            var Q55;
            {var subQ0=sQuery(id+"F0.wireOp",EDGE,"E41.MirrorCS");var subQ12=sQuery(id+"F0.wireOp",EDGE,"E52.MirrorCS");var subQ13=makeQuery(id+"F0.imprint","INTERSECT",VERTEX,{"derivedFrom":[subQ0,subQ12]});Q55=makeQuery(id+"F0.imprint","IMPRINT",FACE,{"disambiguationData":[TD([[makeQuery(id+"F0.imprint","IMPRINT",EDGE,{"disambiguationData":[TD([[subQ13,-1.0]])],"derivedFrom":subQ0}),1.0]])]});}
            var Q56;
            {var subQ0=sQuery(id+"F0.wireOp",EDGE,"E51.MirrorCS");Q56=makeQuery(id+"F0.imprint","IMPRINT",FACE,{"disambiguationData":[TD([[makeQuery(id+"F0.imprint","IMPRINT",EDGE,{"derivedFrom":subQ0}),1.0]])]});}
            var Q57;
            {var subQ0=sQuery(id+"F0.wireOp",EDGE,"E48.MirrorCS");Q57=makeQuery(id+"F0.imprint","IMPRINT",FACE,{"disambiguationData":[TD([[makeQuery(id+"F0.imprint","IMPRINT",EDGE,{"derivedFrom":subQ0}),1.0]])]});}
            var Q58;
            {var subQ0=sQuery(id+"F0.wireOp",EDGE,"E50.MirrorCS");Q58=makeQuery(id+"F0.imprint","IMPRINT",FACE,{"disambiguationData":[TD([[makeQuery(id+"F0.imprint","IMPRINT",EDGE,{"derivedFrom":subQ0}),1.0]])]});}
            var Q59;
            {var subQ0=sQuery(id+"F0.wireOp",EDGE,"E42.MirrorCS");Q59=makeQuery(id+"F0.imprint","IMPRINT",FACE,{"disambiguationData":[TD([[makeQuery(id+"F0.imprint","IMPRINT",EDGE,{"derivedFrom":subQ0}),-1.0]])]});}
            var Q60;
            {var subQ0=sQuery(id+"F0.wireOp",EDGE,"E44.MirrorCS");Q60=makeQuery(id+"F0.imprint","IMPRINT",FACE,{"disambiguationData":[TD([[makeQuery(id+"F0.imprint","IMPRINT",EDGE,{"derivedFrom":subQ0}),-1.0]])]});}
            var Q61;
            {var subQ1=sQuery(id+"F0.wireOp",EDGE,"E5.bottom");Q61=makeQuery(id+"F0.imprint","IMPRINT",FACE,{"disambiguationData":[TD([[makeQuery(id+"F0.imprint","IMPRINT",EDGE,{"derivedFrom":subQ1}),-1.0]])]});}
            var Q62;
            {var subQ3=sQuery(id+"F0.wireOp",EDGE,"E45.MirrorCS");Q62=makeQuery(id+"F0.imprint","IMPRINT",FACE,{"disambiguationData":[TD([[makeQuery(id+"F0.imprint","IMPRINT",EDGE,{"derivedFrom":subQ3}),1.0]])]});}
            var Q63;
            Q63=makeQuery(id+"F0.imprint","IMPRINT",FACE,{"disambiguationData":[TD([[makeQuery(id+"F0.imprint","IMPRINT",EDGE,{"derivedFrom":sQuery(id+"F0.wireOp",EDGE,"E2.bottom")}),1.0]])]});
            var Q64;
            Q64=makeQuery(id+"F0.imprint","IMPRINT",FACE,{"disambiguationData":[TD([[makeQuery(id+"F0.imprint","IMPRINT",EDGE,{"derivedFrom":sQuery(id+"F0.wireOp",EDGE,"E92.bottom")}),-1.0]])]});
            var Q65;
            {var subQ4=sQuery(id+"F0.wireOp",EDGE,"E43.MirrorCS");Q65=makeQuery(id+"F0.imprint","IMPRINT",FACE,{"disambiguationData":[TD([[makeQuery(id+"F0.imprint","IMPRINT",EDGE,{"derivedFrom":subQ4}),1.0]])]});}
            var Q66;
            Q66=makeQuery(id+"F0.imprint","IMPRINT",FACE,{"disambiguationData":[TD([[makeQuery(id+"F0.imprint","IMPRINT",EDGE,{"derivedFrom":sQuery(id+"F0.wireOp",EDGE,"E90.bottom")}),-1.0]])]});
            var Q67;
            {var subQ4=sQuery(id+"F0.wireOp",EDGE,"vQMFGzFv-Y8NP-JtpC-7Ezq-OnBZfbkepPW4.top");Q67=makeQuery(id+"F0.imprint","IMPRINT",FACE,{"disambiguationData":[TD([[makeQuery(id+"F0.imprint","IMPRINT",EDGE,{"derivedFrom":subQ4}),-1.0]])]});}
            var Q68;
            Q68=makeQuery(id+"F0.imprint","IMPRINT",FACE,{"disambiguationData":[TD([[makeQuery(id+"F0.imprint","IMPRINT",EDGE,{"derivedFrom":sQuery(id+"F0.wireOp",EDGE,"LMotzGq9-rada-kq9y-cdnF-zIBoFce3W3Eb.top")}),-1.0]])]});
            var Q69;
            {var subQ0=sQuery(id+"F0.wireOp",EDGE,"N8sRs5Oq-EvWD-7U19-JG4P-MgaPDmZcmoIZ.left");Q69=makeQuery(id+"F0.imprint","IMPRINT",FACE,{"disambiguationData":[TD([[makeQuery(id+"F0.imprint","IMPRINT",EDGE,{"derivedFrom":subQ0}),-1.0]])]});}
            var Q70;
            Q70=makeQuery(id+"F0.imprint","IMPRINT",FACE,{"disambiguationData":[TD([[makeQuery(id+"F0.imprint","IMPRINT",EDGE,{"derivedFrom":sQuery(id+"F0.wireOp",EDGE,"jhdKA4KA-ir7Y-VsJP-fwj5-G50ZXv2MpHBA.bottom")}),1.0]])]});
            var Q71;
            {var subQ0=sQuery(id+"F0.wireOp",EDGE,"97e8bb4e-b4ea-4c57-9eba-86354fd999400.MirrorCS");Q71=makeQuery(id+"F0.imprint","IMPRINT",FACE,{"disambiguationData":[TD([[makeQuery(id+"F0.imprint","IMPRINT",EDGE,{"derivedFrom":subQ0}),1.0]])]});}
            var Q72;
            {var subQ3=sQuery(id+"F0.wireOp",EDGE,"E93.bottom");Q72=makeQuery(id+"F0.imprint","IMPRINT",FACE,{"disambiguationData":[TD([[makeQuery(id+"F0.imprint","IMPRINT",EDGE,{"derivedFrom":subQ3}),-1.0]])]});}
            var Q73;
            Q73=makeQuery(id+"F0.imprint","IMPRINT",FACE,{"disambiguationData":[TD([[makeQuery(id+"F0.imprint","IMPRINT",EDGE,{"derivedFrom":sQuery(id+"F0.wireOp",EDGE,"E110.MirrorCS")}),1.0]])]});
            var Q74;
            {var subQ0=sQuery(id+"F0.wireOp",EDGE,"E76.MirrorCS");Q74=makeQuery(id+"F0.imprint","IMPRINT",FACE,{"disambiguationData":[TD([[makeQuery(id+"F0.imprint","IMPRINT",EDGE,{"derivedFrom":subQ0}),-1.0]])]});}
            var Q75;
            {var subQ0=sQuery(id+"F0.wireOp",EDGE,"E84.MirrorCS");var subQ12=sQuery(id+"F0.wireOp",EDGE,"E18.MirrorCS");var subQ14=makeQuery(id+"F0.imprint","INTERSECT",VERTEX,{"derivedFrom":[subQ0,subQ12]});Q75=makeQuery(id+"F0.imprint","IMPRINT",FACE,{"disambiguationData":[TD([[makeQuery(id+"F0.imprint","IMPRINT",EDGE,{"disambiguationData":[TD([[subQ14,-1.0]])],"derivedFrom":subQ0}),-1.0]])]});}
            var Q76;
            {var subQ0=sQuery(id+"F0.wireOp",EDGE,"E77.MirrorCS");Q76=makeQuery(id+"F0.imprint","IMPRINT",FACE,{"disambiguationData":[TD([[makeQuery(id+"F0.imprint","IMPRINT",EDGE,{"derivedFrom":subQ0}),1.0]])]});}
            var Q77;
            {var subQ0=sQuery(id+"F0.wireOp",EDGE,"E80.MirrorCS");Q77=makeQuery(id+"F0.imprint","IMPRINT",FACE,{"disambiguationData":[TD([[makeQuery(id+"F0.imprint","IMPRINT",EDGE,{"derivedFrom":subQ0}),-1.0]])]});}
            var Q78;
            {var subQ0=sQuery(id+"F0.wireOp",EDGE,"E81.MirrorCS");Q78=makeQuery(id+"F0.imprint","IMPRINT",FACE,{"disambiguationData":[TD([[makeQuery(id+"F0.imprint","IMPRINT",EDGE,{"derivedFrom":subQ0}),-1.0]])]});}
            var Q79;
            {var subQ0=sQuery(id+"F0.wireOp",EDGE,"E78.MirrorCS");Q79=makeQuery(id+"F0.imprint","IMPRINT",FACE,{"disambiguationData":[TD([[makeQuery(id+"F0.imprint","IMPRINT",EDGE,{"derivedFrom":subQ0}),-1.0]])]});}
            var Q80;
            {var subQ3=sQuery(id+"F0.wireOp",EDGE,"E86.MirrorCS");Q80=makeQuery(id+"F0.imprint","IMPRINT",FACE,{"disambiguationData":[TD([[makeQuery(id+"F0.imprint","IMPRINT",EDGE,{"derivedFrom":subQ3}),1.0]])]});}
            var Q81;
            {var subQ4=sQuery(id+"F0.wireOp",EDGE,"E14.MirrorCS");Q81=makeQuery(id+"F0.imprint","IMPRINT",FACE,{"disambiguationData":[TD([[makeQuery(id+"F0.imprint","IMPRINT",EDGE,{"derivedFrom":subQ4}),-1.0]])]});}
            var Q82;
            {var subQ9=sQuery(id+"F0.wireOp",EDGE,"c5a5b527-27a6-4c28-9b58-9e48672ab9af27.MirrorCS");var subQ10=sQuery(id+"F0.wireOp",EDGE,"E16.MirrorCS");var subQ11=makeQuery(id+"F0.imprint","INTERSECT",VERTEX,{"derivedFrom":[subQ10,subQ9]});Q82=makeQuery(id+"F0.imprint","IMPRINT",FACE,{"disambiguationData":[TD([[makeQuery(id+"F0.imprint","IMPRINT",EDGE,{"disambiguationData":[TD([[subQ11,-1.0]])],"derivedFrom":subQ9}),1.0]])]});}
            var Q83;
            Q83=makeQuery(id+"F0.imprint","IMPRINT",FACE,{"disambiguationData":[TD([[makeQuery(id+"F0.imprint","IMPRINT",EDGE,{"derivedFrom":sQuery(id+"F0.wireOp",EDGE,"gwfFcFAY-4S5T-gqrI-loYC-4U2pHZFZRN9T.bottom")}),1.0]])]});
            var Q84;
            Q84=makeQuery(id+"F0.imprint","IMPRINT",FACE,{"disambiguationData":[TD([[makeQuery(id+"F0.imprint","IMPRINT",EDGE,{"derivedFrom":sQuery(id+"F0.wireOp",EDGE,"E91.bottom")}),-1.0]])]});
            var Q85;
            Q85=makeQuery(id+"F0.imprint","IMPRINT",FACE,{"disambiguationData":[TD([[makeQuery(id+"F0.imprint","IMPRINT",EDGE,{"derivedFrom":sQuery(id+"F0.wireOp",EDGE,"gg605cFh-yEl2-BISW-pC2I-Yae126qmmnOe.bottom")}),-1.0]])]});
            var Q86;
            Q86=makeQuery(id+"F0.imprint","IMPRINT",FACE,{"disambiguationData":[TD([[makeQuery(id+"F0.imprint","IMPRINT",EDGE,{"derivedFrom":sQuery(id+"F0.wireOp",EDGE,"E94.top")}),1.0]])]});
            var Q87;
            {var subQ5=sQuery(id+"F0.wireOp",EDGE,"E19.right");Q87=makeQuery(id+"F0.imprint","IMPRINT",FACE,{"disambiguationData":[TD([[makeQuery(id+"F0.imprint","IMPRINT",EDGE,{"derivedFrom":subQ5}),-1.0]])]});}
            var Q88;
            {var subQ5=sQuery(id+"F0.wireOp",EDGE,"E5.left");Q88=makeQuery(id+"F0.imprint","IMPRINT",FACE,{"disambiguationData":[TD([[makeQuery(id+"F0.imprint","IMPRINT",EDGE,{"derivedFrom":subQ5}),1.0]])]});}
            var Q89;
            {var subQ2=sQuery(id+"F0.wireOp",EDGE,"E4.left");Q89=makeQuery(id+"F0.imprint","IMPRINT",FACE,{"disambiguationData":[TD([[makeQuery(id+"F0.imprint","IMPRINT",EDGE,{"derivedFrom":subQ2}),1.0]])]});}
            var Q90;
            {var subQ2=sQuery(id+"F0.wireOp",EDGE,"E20.left");Q90=makeQuery(id+"F0.imprint","IMPRINT",FACE,{"disambiguationData":[TD([[makeQuery(id+"F0.imprint","IMPRINT",EDGE,{"derivedFrom":subQ2}),1.0]])]});}
            var Q91;
            {var subQ0=sQuery(id+"F0.wireOp",EDGE,"E47.MirrorCS");var subQ12=makeQuery(id+"F0.imprint","INTERSECT",VERTEX,{"derivedFrom":[sQuery(id+"F0.wireOp",EDGE,"E45.MirrorCS"),subQ0]});Q91=makeQuery(id+"F0.imprint","IMPRINT",FACE,{"disambiguationData":[TD([[makeQuery(id+"F0.imprint","IMPRINT",EDGE,{"disambiguationData":[TD([[subQ12,1.0]])],"derivedFrom":subQ0}),-1.0]])]});}
            var Q92;
            {var subQ3=sQuery(id+"F0.wireOp",EDGE,"E97.bottom");Q92=makeQuery(id+"F0.imprint","IMPRINT",FACE,{"disambiguationData":[TD([[makeQuery(id+"F0.imprint","IMPRINT",EDGE,{"derivedFrom":subQ3}),-1.0]])]});}
            var Q93;
            {var subQ0=sQuery(id+"F0.wireOp",EDGE,"E96.top");Q93=makeQuery(id+"F0.imprint","IMPRINT",FACE,{"disambiguationData":[TD([[makeQuery(id+"F0.imprint","IMPRINT",EDGE,{"derivedFrom":subQ0}),-1.0]])]});}
            var Q94;
            {var subQ1=sQuery(id+"F0.wireOp",EDGE,"E100.left");Q94=makeQuery(id+"F0.imprint","IMPRINT",FACE,{"disambiguationData":[TD([[makeQuery(id+"F0.imprint","IMPRINT",EDGE,{"derivedFrom":subQ1}),1.0]])]});}
            var Q95;
            Q95=makeQuery(id+"F0.imprint","IMPRINT",FACE,{"disambiguationData":[TD([[makeQuery(id+"F0.imprint","IMPRINT",EDGE,{"derivedFrom":sQuery(id+"F0.wireOp",EDGE,"E103.bottom")}),-1.0]])]});
            var Q96;
            Q96=makeQuery(id+"F0.imprint","IMPRINT",FACE,{"disambiguationData":[TD([[makeQuery(id+"F0.imprint","IMPRINT",EDGE,{"derivedFrom":sQuery(id+"F0.wireOp",EDGE,"E102.bottom")}),1.0]])]});
            var Q97;
            {var subQ0=sQuery(id+"F0.wireOp",EDGE,"E105.MirrorCS");Q97=makeQuery(id+"F0.imprint","IMPRINT",FACE,{"disambiguationData":[TD([[makeQuery(id+"F0.imprint","IMPRINT",EDGE,{"derivedFrom":subQ0}),-1.0]])]});}
            var Q98;
            {var subQ3=sQuery(id+"F0.wireOp",EDGE,"E99.bottom");Q98=makeQuery(id+"F0.imprint","IMPRINT",FACE,{"disambiguationData":[TD([[makeQuery(id+"F0.imprint","IMPRINT",EDGE,{"derivedFrom":subQ3}),1.0]])]});}
            var Q99;
            {var subQ0=sQuery(id+"F0.wireOp",EDGE,"E98.top");Q99=makeQuery(id+"F0.imprint","IMPRINT",FACE,{"disambiguationData":[TD([[makeQuery(id+"F0.imprint","IMPRINT",EDGE,{"derivedFrom":subQ0}),1.0]])]});}
            var Q100;
            {var subQ1=sQuery(id+"F0.wireOp",EDGE,"E19.right");Q100=makeQuery(id+"F0.imprint","IMPRINT",FACE,{"disambiguationData":[TD([[makeQuery(id+"F0.imprint","IMPRINT",EDGE,{"derivedFrom":subQ1}),1.0]])]});}
            var Q101;
            {var subQ0=sQuery(id+"F0.wireOp",EDGE,"E85.MirrorCS");Q101=makeQuery(id+"F0.imprint","IMPRINT",FACE,{"disambiguationData":[TD([[makeQuery(id+"F0.imprint","IMPRINT",EDGE,{"derivedFrom":subQ0}),-1.0]])]});}
            var Q102;
            Q102=makeQuery(id+"F0.imprint","IMPRINT",FACE,{"disambiguationData":[TD([[makeQuery(id+"F0.imprint","IMPRINT",EDGE,{"derivedFrom":sQuery(id+"F0.wireOp",EDGE,"E109.bottom")}),1.0]])]});
            var Q103;
            {var subQ0=sQuery(id+"F0.wireOp",EDGE,"E0.left");Q103=makeQuery(id+"F0.imprint","IMPRINT",FACE,{"disambiguationData":[TD([[makeQuery(id+"F0.imprint","IMPRINT",EDGE,{"derivedFrom":subQ0}),1.0]])]});}
            var Q104;
            {var subQ7=sQuery(id+"F0.wireOp",EDGE,"E74.MirrorCS");Q104=makeQuery(id+"F0.imprint","IMPRINT",FACE,{"disambiguationData":[TD([[makeQuery(id+"F0.imprint","IMPRINT",EDGE,{"derivedFrom":subQ7}),-1.0]])]});}
            var Q105;
            {var subQ5=sQuery(id+"F0.wireOp",EDGE,"RUY86IJm-eIA6-erxx-gF4t-aafXN3xHqDuE.bottom");Q105=makeQuery(id+"F0.imprint","IMPRINT",FACE,{"disambiguationData":[TD([[makeQuery(id+"F0.imprint","IMPRINT",EDGE,{"derivedFrom":subQ5}),-1.0]])]});}
            var Q106;
            {var subQ5=sQuery(id+"F0.wireOp",EDGE,"cn2VBdXs-QnGU-n3qP-ujRz-xjExlO5BVOZB.top");Q106=makeQuery(id+"F0.imprint","IMPRINT",FACE,{"disambiguationData":[TD([[makeQuery(id+"F0.imprint","IMPRINT",EDGE,{"derivedFrom":subQ5}),1.0]])]});}
            var Q107;
            {var subQ5=sQuery(id+"F0.wireOp",EDGE,"cn2VBdXs-QnGU-n3qP-ujRz-xjExlO5BVOZB.bottom");Q107=makeQuery(id+"F0.imprint","IMPRINT",FACE,{"disambiguationData":[TD([[makeQuery(id+"F0.imprint","IMPRINT",EDGE,{"derivedFrom":subQ5}),-1.0]])]});}
            var Q108;
            {var subQ5=sQuery(id+"F0.wireOp",EDGE,"RUY86IJm-eIA6-erxx-gF4t-aafXN3xHqDuE.top");Q108=makeQuery(id+"F0.imprint","IMPRINT",FACE,{"disambiguationData":[TD([[makeQuery(id+"F0.imprint","IMPRINT",EDGE,{"derivedFrom":subQ5}),1.0]])]});}
            var Q109;
            Q109=makeQuery(id+"F0.imprint","IMPRINT",FACE,{"disambiguationData":[TD([[makeQuery(id+"F0.imprint","IMPRINT",EDGE,{"derivedFrom":sQuery(id+"F0.wireOp",EDGE,"Bj6PZoOF-mrB7-ptqh-beZS-oW6ks2iHURm3.top")}),-1.0]])]});
            var Q110;
            Q110=makeQuery(id+"F0.imprint","IMPRINT",FACE,{"disambiguationData":[TD([[makeQuery(id+"F0.imprint","IMPRINT",EDGE,{"derivedFrom":sQuery(id+"F0.wireOp",EDGE,"tIshytMV-MwIu-Psvy-HpBG-QoDstqUTy8cI.bottom")}),-1.0]])]});
            var Q111;
            Q111=makeQuery(id+"F0.imprint","IMPRINT",FACE,{"disambiguationData":[TD([[makeQuery(id+"F0.imprint","IMPRINT",EDGE,{"derivedFrom":sQuery(id+"F0.wireOp",EDGE,"xB6JHSH8-4uVH-Gtdu-1WNn-2dnqj1t1gMDK.bottom")}),-1.0]])]});
            var Q112;
            Q112=makeQuery(id+"F0.imprint","IMPRINT",FACE,{"disambiguationData":[TD([[makeQuery(id+"F0.imprint","IMPRINT",EDGE,{"derivedFrom":sQuery(id+"F0.wireOp",EDGE,"8446fafe-80e3-4871-9202-4563462575e50.MirrorCS")}),-1.0]])]});
            var Q113;
            {var subQ0=sQuery(id+"F0.wireOp",EDGE,"E90.left");Q113=makeQuery(id+"F0.imprint","IMPRINT",FACE,{"disambiguationData":[TD([[makeQuery(id+"F0.imprint","IMPRINT",EDGE,{"derivedFrom":subQ0}),1.0]])]});}
            var Q114;
            Q114=makeQuery(id+"F0.imprint","IMPRINT",FACE,{"disambiguationData":[TD([[makeQuery(id+"F0.imprint","IMPRINT",EDGE,{"derivedFrom":sQuery(id+"F0.wireOp",EDGE,"52DiRzlL-i6Ps-kMCr-3Wpo-19FTAjKvPZNU.bottom")}),-1.0]])]});
            var Q115;
            {var subQ3=sQuery(id+"F0.wireOp",EDGE,"E90.left");Q115=makeQuery(id+"F0.imprint","IMPRINT",FACE,{"disambiguationData":[TD([[makeQuery(id+"F0.imprint","IMPRINT",EDGE,{"derivedFrom":subQ3}),-1.0]])]});}
            var Q116;
            Q116=makeQuery(id+"F0.imprint","IMPRINT",FACE,{"disambiguationData":[TD([[makeQuery(id+"F0.imprint","IMPRINT",EDGE,{"derivedFrom":sQuery(id+"F0.wireOp",EDGE,"sMOzYcuG-WELo-MGud-Y4Io-L2SvrtbJ6jsE.bottom")}),-1.0]])]});
            var Q117;
            Q117=makeQuery(id+"F0.imprint","IMPRINT",FACE,{"disambiguationData":[TD([[makeQuery(id+"F0.imprint","IMPRINT",EDGE,{"derivedFrom":sQuery(id+"F0.wireOp",EDGE,"E112.top")}),1.0]])]});
            var Q118;
            {var subQ0=sQuery(id+"F0.wireOp",EDGE,"E113.left");Q118=makeQuery(id+"F0.imprint","IMPRINT",FACE,{"disambiguationData":[TD([[makeQuery(id+"F0.imprint","IMPRINT",EDGE,{"derivedFrom":subQ0}),-1.0]])]});}
            var Q119;
            Q119=makeQuery(id+"F0.imprint","IMPRINT",FACE,{"disambiguationData":[TD([[makeQuery(id+"F0.imprint","IMPRINT",EDGE,{"derivedFrom":sQuery(id+"F0.wireOp",EDGE,"E118.bottom")}),1.0]])]});
            var Q120;
            Q120=makeQuery(id+"F0.imprint","IMPRINT",FACE,{"disambiguationData":[TD([[makeQuery(id+"F0.imprint","IMPRINT",EDGE,{"derivedFrom":sQuery(id+"F0.wireOp",EDGE,"E117.bottom")}),-1.0]])]});
            var Q121;
            Q121=makeQuery(id+"F0.imprint","IMPRINT",FACE,{"disambiguationData":[TD([[makeQuery(id+"F0.imprint","IMPRINT",EDGE,{"derivedFrom":sQuery(id+"F0.wireOp",EDGE,"E120.MirrorCS")}),1.0]])]});
            var Q122;
            {var subQ3=sQuery(id+"F0.wireOp",EDGE,"E115.bottom");Q122=makeQuery(id+"F0.imprint","IMPRINT",FACE,{"disambiguationData":[TD([[makeQuery(id+"F0.imprint","IMPRINT",EDGE,{"derivedFrom":subQ3}),-1.0]])]});}
            var Q123;
            {var subQ0=sQuery(id+"F0.wireOp",EDGE,"E115.left");var subQ5=sQuery(id+"F0.wireOp",EDGE,"E113.bottom");var subQ6=makeQuery(id+"F0.imprint","INTERSECT",VERTEX,{"derivedFrom":[subQ5,subQ0]});Q123=makeQuery(id+"F0.imprint","IMPRINT",FACE,{"disambiguationData":[TD([[makeQuery(id+"F0.imprint","IMPRINT",EDGE,{"disambiguationData":[TD([[subQ6,1.0]])],"derivedFrom":subQ5}),-1.0]])]});}
            var Q124;
            Q124=makeQuery(id+"F0.imprint","IMPRINT",FACE,{"disambiguationData":[TD([[makeQuery(id+"F0.imprint","IMPRINT",EDGE,{"derivedFrom":sQuery(id+"F0.wireOp",EDGE,"E125.bottom")}),-1.0]])]});
            var Q125;
            {var subQ8=sQuery(id+"F0.wireOp",EDGE,"E91.right");Q125=makeQuery(id+"F0.imprint","IMPRINT",FACE,{"disambiguationData":[TD([[makeQuery(id+"F0.imprint","IMPRINT",EDGE,{"derivedFrom":subQ8}),-1.0]])]});}
            var Q126;
            {var subQ0=sQuery(id+"F0.wireOp",EDGE,"E115.top");Q126=makeQuery(id+"F0.imprint","IMPRINT",FACE,{"disambiguationData":[TD([[makeQuery(id+"F0.imprint","IMPRINT",EDGE,{"derivedFrom":subQ0}),-1.0]])]});}
            extrude(context, id + "F1", {"entities" : qUnion([Q0, Q1, Q2, Q3, Q4, Q5, Q6, Q7, Q8, Q9, Q10, Q11, Q12, Q13, Q14, Q15, Q16, Q17, Q18, Q19, Q20, Q21, Q22, Q23, Q24, Q25, Q26, Q27, Q28, Q29, Q30, Q31, Q32, Q33, Q34, Q35, Q36, Q37, Q38, Q39, Q40, Q41, Q42, Q43, Q44, Q45, Q46, Q47, Q48, Q49, Q50, Q51, Q52, Q53, Q54, Q55, Q56, Q57, Q58, Q59, Q60, Q61, Q62, Q63, Q64, Q65, Q66, Q67, Q68, Q69, Q70, Q71, Q72, Q73, Q74, Q75, Q76, Q77, Q78, Q79, Q80, Q81, Q82, Q83, Q84, Q85, Q86, Q87, Q88, Q89, Q90, Q91, Q92, Q93, Q94, Q95, Q96, Q97, Q98, Q99, Q100, Q101, Q102, Q103, Q104, Q105, Q106, Q107, Q108, Q109, Q110, Q111, Q112, Q113, Q114, Q115, Q116, Q117, Q118, Q119, Q120, Q121, Q122, Q123, Q124, Q125, Q126]), "offsetDistance" : 30.48 * mm, "depth" : ((3 + 1.5) / 12) * mm});
        }
        {
            var Q0;
            Q0=makeQuery(id+"F1.opExtrude","SWEPT_FACE",FACE,{"disambiguationData":[OSD([sQuery(id+"F0.wireOp",EDGE,"E2.bottom"),sQuery(id+"F0.wireOp",EDGE,"E94.top")])]});
            var sketch = newSketch(context, id + "F2", { "sketchPlane" : qUnion([Q0])});
            skLineSegment(sketch, "E127.bottom", {"start": v(-3683.16, 114.3) * mm, "end": v(-1823.68, 114.3) * mm});
            skLineSegment(sketch, "E127.top", {"start": v(-3683.16, 76.2) * mm, "end": v(-1823.68, 76.2) * mm});
            skLineSegment(sketch, "E127.left", {"start": v(-3683.16, 114.3) * mm, "end": v(-3683.16, 76.2) * mm});
            skLineSegment(sketch, "E127.right", {"start": v(-1823.68, 114.3) * mm, "end": v(-1823.68, 76.2) * mm});
            skLineSegment(sketch, "E128.bottom", {"start": v(-1683.98, 114.3) * mm, "end": v(175.6, 114.3) * mm});
            skLineSegment(sketch, "E128.top", {"start": v(-1683.98, 76.2) * mm, "end": v(175.6, 76.2) * mm});
            skLineSegment(sketch, "E128.left", {"start": v(-1683.98, 114.3) * mm, "end": v(-1683.98, 76.2) * mm});
            skLineSegment(sketch, "E128.right", {"start": v(175.6, 114.3) * mm, "end": v(175.6, 76.2) * mm});
            skLineSegment(sketch, "E129.bottom", {"start": v(315.2, 114.3) * mm, "end": v(2174.8, 114.3) * mm});
            skLineSegment(sketch, "E129.top", {"start": v(315.2, 76.2) * mm, "end": v(2174.8, 76.2) * mm});
            skLineSegment(sketch, "E129.left", {"start": v(315.2, 114.3) * mm, "end": v(315.2, 76.2) * mm});
            skLineSegment(sketch, "E129.right", {"start": v(2174.8, 114.3) * mm, "end": v(2174.8, 76.2) * mm});
            skLineSegment(sketch, "E130.bottom", {"start": v(2314.39, 114.3) * mm, "end": v(4173.97, 114.3) * mm});
            skLineSegment(sketch, "E130.top", {"start": v(2314.39, 76.2) * mm, "end": v(4173.97, 76.2) * mm});
            skLineSegment(sketch, "E130.left", {"start": v(2314.39, 114.3) * mm, "end": v(2314.39, 76.2) * mm});
            skLineSegment(sketch, "E130.right", {"start": v(4173.97, 114.3) * mm, "end": v(4173.97, 76.2) * mm});
            skLineSegment(sketch, "E131.bottom", {"start": v(-3683.16, 0) * mm, "end": v(-1823.68, 0) * mm});
            skLineSegment(sketch, "E131.top", {"start": v(-3683.16, 38.1) * mm, "end": v(-1823.68, 38.1) * mm});
            skLineSegment(sketch, "E131.left", {"start": v(-3683.16, 0) * mm, "end": v(-3683.16, 38.1) * mm});
            skLineSegment(sketch, "E131.right", {"start": v(-1823.68, 0) * mm, "end": v(-1823.68, 38.1) * mm});
            skLineSegment(sketch, "E132.bottom", {"start": v(-1683.98, 0) * mm, "end": v(175.6, 0) * mm});
            skLineSegment(sketch, "E132.top", {"start": v(-1683.98, 38.1) * mm, "end": v(175.6, 38.1) * mm});
            skLineSegment(sketch, "E132.left", {"start": v(-1683.98, 0) * mm, "end": v(-1683.98, 38.1) * mm});
            skLineSegment(sketch, "E132.right", {"start": v(175.6, 0) * mm, "end": v(175.6, 38.1) * mm});
            skPoint(sketch, "E133.firstSnap0", {"position": v(242.45, 0) * mm});
            skLineSegment(sketch, "E133.bottom", {"start": v(315.2, 0) * mm, "end": v(2174.8, 0) * mm});
            skLineSegment(sketch, "E133.top", {"start": v(315.2, 38.1) * mm, "end": v(2174.8, 38.1) * mm});
            skLineSegment(sketch, "E133.left", {"start": v(315.2, 0) * mm, "end": v(315.2, 38.1) * mm});
            skLineSegment(sketch, "E133.right", {"start": v(2174.8, 0) * mm, "end": v(2174.8, 38.1) * mm});
            skLineSegment(sketch, "E134.bottom", {"start": v(2314.39, 0) * mm, "end": v(4173.97, 0) * mm});
            skLineSegment(sketch, "E134.top", {"start": v(2314.39, 38.1) * mm, "end": v(4173.97, 38.1) * mm});
            skLineSegment(sketch, "E134.left", {"start": v(2314.39, 0) * mm, "end": v(2314.39, 38.1) * mm});
            skLineSegment(sketch, "E134.right", {"start": v(4173.97, 0) * mm, "end": v(4173.97, 38.1) * mm});
            skSolve(sketch);
        }
        {
            var Q0;
            Q0=makeQuery(id+"F2.imprint","IMPRINT",FACE,{"disambiguationData":[TD([[makeQuery(id+"F2.imprint","IMPRINT",EDGE,{"derivedFrom":sQuery(id+"F2.wireOp",EDGE,"E131.bottom")}),1.0]])]});
            var Q1;
            Q1=makeQuery(id+"F2.imprint","IMPRINT",FACE,{"disambiguationData":[TD([[makeQuery(id+"F2.imprint","IMPRINT",EDGE,{"derivedFrom":sQuery(id+"F2.wireOp",EDGE,"E132.bottom")}),1.0]])]});
            var Q2;
            Q2=makeQuery(id+"F2.imprint","IMPRINT",FACE,{"disambiguationData":[TD([[makeQuery(id+"F2.imprint","IMPRINT",EDGE,{"derivedFrom":sQuery(id+"F2.wireOp",EDGE,"E133.bottom")}),1.0]])]});
            var Q3;
            Q3=makeQuery(id+"F2.imprint","IMPRINT",FACE,{"disambiguationData":[TD([[makeQuery(id+"F2.imprint","IMPRINT",EDGE,{"derivedFrom":sQuery(id+"F2.wireOp",EDGE,"E134.bottom")}),1.0]])]});
            extrude(context, id + "F3", {"entities" : qUnion([Q0, Q1, Q2, Q3]), "operationType" : NewBodyOperationType.REMOVE, "oppositeDirection" : true, "depth" : 3657.6 * mm, "offsetDistance" : 30.48 * mm});
        }
    });
